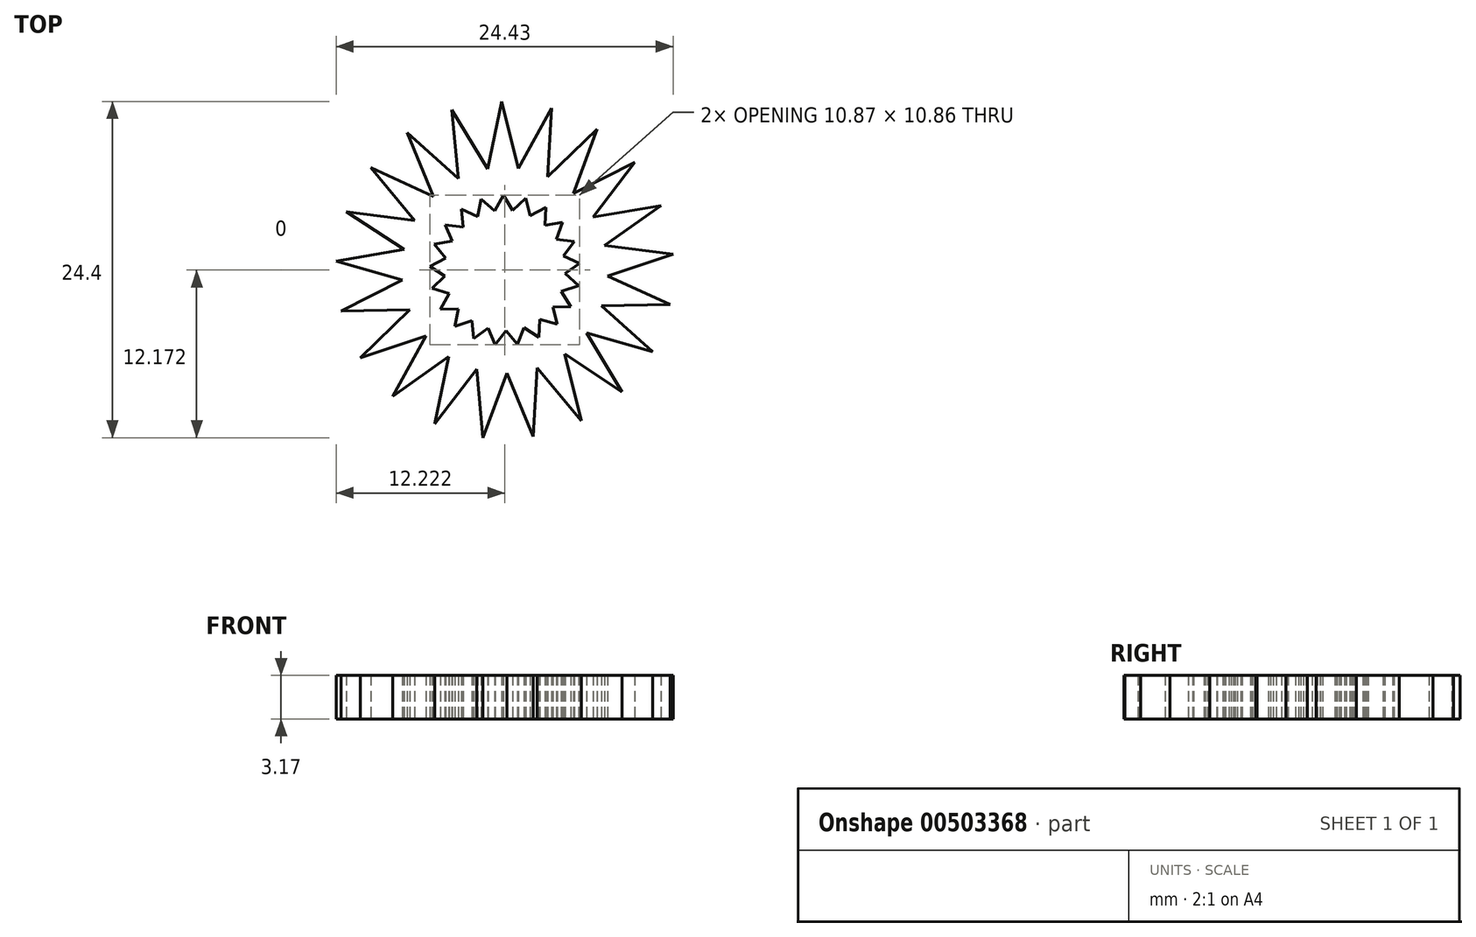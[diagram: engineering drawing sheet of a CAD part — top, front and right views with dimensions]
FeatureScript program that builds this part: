
annotation { "Feature Type Name" : "Feature", "Feature Type Description" : "" }
export const myFeature = defineFeature(function(context is Context, id is Id, definition is map)
    precondition{}
    {
        {
            var Q0;
            Q0=qCreatedBy(makeId("Top.planeOp"),FACE);
            var sketch = newSketch(context, id + "F0", { "sketchPlane" : qUnion([Q0])});
            skLineSegment(sketch, "E0", {"start": v(-5.1, -11.14) * mm, "end": v(-0.24, 12.25) * mm});
            skLineSegment(sketch, "E1", {"start": v(-0.24, 12.25) * mm, "end": v(5.54, -10.93) * mm});
            skLineSegment(sketch, "E2", {"start": v(5.54, -10.93) * mm, "end": v(-9.73, 7.45) * mm});
            skLineSegment(sketch, "E3", {"start": v(-9.73, 7.45) * mm, "end": v(12, -2.49) * mm});
            skLineSegment(sketch, "E4", {"start": v(12, -2.49) * mm, "end": v(-11.89, -2.96) * mm});
            skLineSegment(sketch, "E5", {"start": v(-11.89, -2.96) * mm, "end": v(9.43, 7.83) * mm});
            skLineSegment(sketch, "E6", {"start": v(9.43, 7.83) * mm, "end": v(-5.1, -11.14) * mm});
            skLineSegment(sketch, "E7", {"start": v(-10.49, -6.34) * mm, "end": v(6.7, 10.26) * mm});
            skLineSegment(sketch, "E8", {"start": v(6.7, 10.26) * mm, "end": v(-1.58, -12.15) * mm});
            skLineSegment(sketch, "E9", {"start": v(-1.58, -12.15) * mm, "end": v(-3.84, 11.63) * mm});
            skLineSegment(sketch, "E10", {"start": v(-3.84, 11.63) * mm, "end": v(8.51, -8.81) * mm});
            skLineSegment(sketch, "E11", {"start": v(8.51, -8.81) * mm, "end": v(-11.5, 4.25) * mm});
            skLineSegment(sketch, "E12", {"start": v(-11.5, 4.25) * mm, "end": v(12.2, 1.16) * mm});
            skLineSegment(sketch, "E13", {"start": v(12.2, 1.16) * mm, "end": v(-10.49, -6.34) * mm});
            skLineSegment(sketch, "E14", {"start": v(-8.15, -9.15) * mm, "end": v(3.38, 11.78) * mm});
            skLineSegment(sketch, "E15", {"start": v(3.38, 11.78) * mm, "end": v(2.07, -12.08) * mm});
            skLineSegment(sketch, "E16", {"start": v(2.07, -12.08) * mm, "end": v(-7.1, 9.98) * mm});
            skLineSegment(sketch, "E17", {"start": v(-7.1, 9.98) * mm, "end": v(10.73, -5.91) * mm});
            skLineSegment(sketch, "E18", {"start": v(10.73, -5.91) * mm, "end": v(-12.23, 0.67) * mm});
            skLineSegment(sketch, "E19", {"start": v(-12.23, 0.67) * mm, "end": v(11.31, 4.7) * mm});
            skLineSegment(sketch, "E20", {"start": v(11.31, 4.7) * mm, "end": v(-8.15, -9.15) * mm});
            skSolve(sketch);
        }
        {
            var Q0;
            {var subQ0=sQuery(id+"F0.wireOp",EDGE,"E7");var subQ1=sQuery(id+"F0.wireOp",EDGE,"E4");var subQ2=makeQuery(id+"F0.imprint","INTERSECT",VERTEX,{"derivedFrom":[subQ1,subQ0]});Q0=makeQuery(id+"F0.imprint","IMPRINT",FACE,{"disambiguationData":[TD([[makeQuery(id+"F0.imprint","IMPRINT",EDGE,{"disambiguationData":[TD([[subQ2,1.0]])],"derivedFrom":subQ1}),1.0]])]});}
            var Q1;
            {var subQ0=sQuery(id+"F0.wireOp",EDGE,"E20");var subQ1=sQuery(id+"F0.wireOp",EDGE,"E0");var subQ2=makeQuery(id+"F0.imprint","INTERSECT",VERTEX,{"derivedFrom":[subQ1,subQ0]});Q1=makeQuery(id+"F0.imprint","IMPRINT",FACE,{"disambiguationData":[TD([[makeQuery(id+"F0.imprint","IMPRINT",EDGE,{"disambiguationData":[TD([[subQ2,-1.0]])],"derivedFrom":subQ1}),1.0]])]});}
            var Q2;
            {var subQ0=sQuery(id+"F0.wireOp",EDGE,"E6");var subQ1=sQuery(id+"F0.wireOp",EDGE,"E0");var subQ2=makeQuery(id+"F0.imprint","INTERSECT",VERTEX,{"derivedFrom":[subQ1,subQ0]});Q2=makeQuery(id+"F0.imprint","IMPRINT",FACE,{"disambiguationData":[TD([[makeQuery(id+"F0.imprint","IMPRINT",EDGE,{"disambiguationData":[TD([[subQ2,-1.0]])],"derivedFrom":subQ1}),-1.0]])]});}
            var Q3;
            {var subQ0=sQuery(id+"F0.wireOp",EDGE,"E9");var subQ1=sQuery(id+"F0.wireOp",EDGE,"E6");var subQ2=makeQuery(id+"F0.imprint","INTERSECT",VERTEX,{"derivedFrom":[subQ1,subQ0]});Q3=makeQuery(id+"F0.imprint","IMPRINT",FACE,{"disambiguationData":[TD([[makeQuery(id+"F0.imprint","IMPRINT",EDGE,{"disambiguationData":[TD([[subQ2,1.0]])],"derivedFrom":subQ1}),1.0]])]});}
            var Q4;
            {var subQ0=sQuery(id+"F0.wireOp",EDGE,"E2");var subQ1=sQuery(id+"F0.wireOp",EDGE,"E1");var subQ2=makeQuery(id+"F0.imprint","INTERSECT",VERTEX,{"derivedFrom":[subQ1,subQ0]});Q4=makeQuery(id+"F0.imprint","IMPRINT",FACE,{"disambiguationData":[TD([[makeQuery(id+"F0.imprint","IMPRINT",EDGE,{"disambiguationData":[TD([[subQ2,1.0]])],"derivedFrom":subQ1}),-1.0]])]});}
            var Q5;
            {var subQ0=sQuery(id+"F0.wireOp",EDGE,"E11");var subQ1=sQuery(id+"F0.wireOp",EDGE,"E1");var subQ2=makeQuery(id+"F0.imprint","INTERSECT",VERTEX,{"derivedFrom":[subQ1,subQ0]});Q5=makeQuery(id+"F0.imprint","IMPRINT",FACE,{"disambiguationData":[TD([[makeQuery(id+"F0.imprint","IMPRINT",EDGE,{"disambiguationData":[TD([[subQ2,1.0]])],"derivedFrom":subQ1}),1.0]])]});}
            var Q6;
            {var subQ0=sQuery(id+"F0.wireOp",EDGE,"E17");var subQ1=sQuery(id+"F0.wireOp",EDGE,"E4");var subQ2=makeQuery(id+"F0.imprint","INTERSECT",VERTEX,{"derivedFrom":[subQ1,subQ0]});Q6=makeQuery(id+"F0.imprint","IMPRINT",FACE,{"disambiguationData":[TD([[makeQuery(id+"F0.imprint","IMPRINT",EDGE,{"disambiguationData":[TD([[subQ2,-1.0]])],"derivedFrom":subQ1}),1.0]])]});}
            var Q7;
            {var subQ0=sQuery(id+"F0.wireOp",EDGE,"E4");var subQ1=sQuery(id+"F0.wireOp",EDGE,"E3");var subQ2=makeQuery(id+"F0.imprint","INTERSECT",VERTEX,{"derivedFrom":[subQ1,subQ0]});Q7=makeQuery(id+"F0.imprint","IMPRINT",FACE,{"disambiguationData":[TD([[makeQuery(id+"F0.imprint","IMPRINT",EDGE,{"disambiguationData":[TD([[subQ2,1.0]])],"derivedFrom":subQ1}),-1.0]])]});}
            var Q8;
            {var subQ0=sQuery(id+"F0.wireOp",EDGE,"E13");var subQ1=sQuery(id+"F0.wireOp",EDGE,"E3");var subQ2=makeQuery(id+"F0.imprint","INTERSECT",VERTEX,{"derivedFrom":[subQ1,subQ0]});Q8=makeQuery(id+"F0.imprint","IMPRINT",FACE,{"disambiguationData":[TD([[makeQuery(id+"F0.imprint","IMPRINT",EDGE,{"disambiguationData":[TD([[subQ2,1.0]])],"derivedFrom":subQ1}),1.0]])]});}
            var Q9;
            {var subQ0=sQuery(id+"F0.wireOp",EDGE,"E19");var subQ1=sQuery(id+"F0.wireOp",EDGE,"E6");var subQ2=makeQuery(id+"F0.imprint","INTERSECT",VERTEX,{"derivedFrom":[subQ1,subQ0]});Q9=makeQuery(id+"F0.imprint","IMPRINT",FACE,{"disambiguationData":[TD([[makeQuery(id+"F0.imprint","IMPRINT",EDGE,{"disambiguationData":[TD([[subQ2,-1.0]])],"derivedFrom":subQ1}),1.0]])]});}
            var Q10;
            {var subQ0=sQuery(id+"F0.wireOp",EDGE,"E6");var subQ1=sQuery(id+"F0.wireOp",EDGE,"E5");var subQ2=makeQuery(id+"F0.imprint","INTERSECT",VERTEX,{"derivedFrom":[subQ1,subQ0]});Q10=makeQuery(id+"F0.imprint","IMPRINT",FACE,{"disambiguationData":[TD([[makeQuery(id+"F0.imprint","IMPRINT",EDGE,{"disambiguationData":[TD([[subQ2,1.0]])],"derivedFrom":subQ1}),-1.0]])]});}
            var Q11;
            {var subQ0=sQuery(id+"F0.wireOp",EDGE,"E8");var subQ1=sQuery(id+"F0.wireOp",EDGE,"E5");var subQ2=makeQuery(id+"F0.imprint","INTERSECT",VERTEX,{"derivedFrom":[subQ1,subQ0]});Q11=makeQuery(id+"F0.imprint","IMPRINT",FACE,{"disambiguationData":[TD([[makeQuery(id+"F0.imprint","IMPRINT",EDGE,{"disambiguationData":[TD([[subQ2,1.0]])],"derivedFrom":subQ1}),1.0]])]});}
            var Q12;
            {var subQ0=sQuery(id+"F0.wireOp",EDGE,"E14");var subQ1=sQuery(id+"F0.wireOp",EDGE,"E1");var subQ2=makeQuery(id+"F0.imprint","INTERSECT",VERTEX,{"derivedFrom":[subQ1,subQ0]});Q12=makeQuery(id+"F0.imprint","IMPRINT",FACE,{"disambiguationData":[TD([[makeQuery(id+"F0.imprint","IMPRINT",EDGE,{"disambiguationData":[TD([[subQ2,-1.0]])],"derivedFrom":subQ1}),1.0]])]});}
            var Q13;
            {var subQ0=sQuery(id+"F0.wireOp",EDGE,"E1");var subQ1=sQuery(id+"F0.wireOp",EDGE,"E0");var subQ2=makeQuery(id+"F0.imprint","INTERSECT",VERTEX,{"derivedFrom":[subQ1,subQ0]});Q13=makeQuery(id+"F0.imprint","IMPRINT",FACE,{"disambiguationData":[TD([[makeQuery(id+"F0.imprint","IMPRINT",EDGE,{"disambiguationData":[TD([[subQ2,1.0]])],"derivedFrom":subQ1}),-1.0]])]});}
            var Q14;
            {var subQ0=sQuery(id+"F0.wireOp",EDGE,"E10");var subQ1=sQuery(id+"F0.wireOp",EDGE,"E0");var subQ2=makeQuery(id+"F0.imprint","INTERSECT",VERTEX,{"derivedFrom":[subQ1,subQ0]});Q14=makeQuery(id+"F0.imprint","IMPRINT",FACE,{"disambiguationData":[TD([[makeQuery(id+"F0.imprint","IMPRINT",EDGE,{"disambiguationData":[TD([[subQ2,1.0]])],"derivedFrom":subQ1}),1.0]])]});}
            var Q15;
            {var subQ0=sQuery(id+"F0.wireOp",EDGE,"E16");var subQ1=sQuery(id+"F0.wireOp",EDGE,"E3");var subQ2=makeQuery(id+"F0.imprint","INTERSECT",VERTEX,{"derivedFrom":[subQ1,subQ0]});Q15=makeQuery(id+"F0.imprint","IMPRINT",FACE,{"disambiguationData":[TD([[makeQuery(id+"F0.imprint","IMPRINT",EDGE,{"disambiguationData":[TD([[subQ2,-1.0]])],"derivedFrom":subQ1}),1.0]])]});}
            var Q16;
            {var subQ0=sQuery(id+"F0.wireOp",EDGE,"E3");var subQ1=sQuery(id+"F0.wireOp",EDGE,"E2");var subQ2=makeQuery(id+"F0.imprint","INTERSECT",VERTEX,{"derivedFrom":[subQ1,subQ0]});Q16=makeQuery(id+"F0.imprint","IMPRINT",FACE,{"disambiguationData":[TD([[makeQuery(id+"F0.imprint","IMPRINT",EDGE,{"disambiguationData":[TD([[subQ2,1.0]])],"derivedFrom":subQ1}),-1.0]])]});}
            var Q17;
            {var subQ0=sQuery(id+"F0.wireOp",EDGE,"E12");var subQ1=sQuery(id+"F0.wireOp",EDGE,"E2");var subQ2=makeQuery(id+"F0.imprint","INTERSECT",VERTEX,{"derivedFrom":[subQ1,subQ0]});Q17=makeQuery(id+"F0.imprint","IMPRINT",FACE,{"disambiguationData":[TD([[makeQuery(id+"F0.imprint","IMPRINT",EDGE,{"disambiguationData":[TD([[subQ2,1.0]])],"derivedFrom":subQ1}),1.0]])]});}
            var Q18;
            {var subQ0=sQuery(id+"F0.wireOp",EDGE,"E18");var subQ1=sQuery(id+"F0.wireOp",EDGE,"E5");var subQ2=makeQuery(id+"F0.imprint","INTERSECT",VERTEX,{"derivedFrom":[subQ1,subQ0]});Q18=makeQuery(id+"F0.imprint","IMPRINT",FACE,{"disambiguationData":[TD([[makeQuery(id+"F0.imprint","IMPRINT",EDGE,{"disambiguationData":[TD([[subQ2,-1.0]])],"derivedFrom":subQ1}),1.0]])]});}
            var Q19;
            {var subQ0=sQuery(id+"F0.wireOp",EDGE,"E5");var subQ1=sQuery(id+"F0.wireOp",EDGE,"E4");var subQ2=makeQuery(id+"F0.imprint","INTERSECT",VERTEX,{"derivedFrom":[subQ1,subQ0]});Q19=makeQuery(id+"F0.imprint","IMPRINT",FACE,{"disambiguationData":[TD([[makeQuery(id+"F0.imprint","IMPRINT",EDGE,{"disambiguationData":[TD([[subQ2,1.0]])],"derivedFrom":subQ1}),-1.0]])]});}
            var Q20;
            {var subQ0=sQuery(id+"F0.wireOp",EDGE,"E7");var subQ1=sQuery(id+"F0.wireOp",EDGE,"E4");var subQ2=makeQuery(id+"F0.imprint","INTERSECT",VERTEX,{"derivedFrom":[subQ1,subQ0]});Q20=makeQuery(id+"F0.imprint","IMPRINT",FACE,{"disambiguationData":[TD([[makeQuery(id+"F0.imprint","IMPRINT",EDGE,{"disambiguationData":[TD([[subQ2,1.0]])],"derivedFrom":subQ1}),-1.0]])]});}
            var Q21;
            {var subQ0=sQuery(id+"F0.wireOp",EDGE,"E13");var subQ1=sQuery(id+"F0.wireOp",EDGE,"E0");var subQ2=makeQuery(id+"F0.imprint","INTERSECT",VERTEX,{"derivedFrom":[subQ1,subQ0]});Q21=makeQuery(id+"F0.imprint","IMPRINT",FACE,{"disambiguationData":[TD([[makeQuery(id+"F0.imprint","IMPRINT",EDGE,{"disambiguationData":[TD([[subQ2,-1.0]])],"derivedFrom":subQ1}),1.0]])]});}
            var Q22;
            {var subQ0=sQuery(id+"F0.wireOp",EDGE,"E20");var subQ1=sQuery(id+"F0.wireOp",EDGE,"E0");var subQ2=makeQuery(id+"F0.imprint","INTERSECT",VERTEX,{"derivedFrom":[subQ1,subQ0]});Q22=makeQuery(id+"F0.imprint","IMPRINT",FACE,{"disambiguationData":[TD([[makeQuery(id+"F0.imprint","IMPRINT",EDGE,{"disambiguationData":[TD([[subQ2,-1.0]])],"derivedFrom":subQ1}),-1.0]])]});}
            var Q23;
            {var subQ0=sQuery(id+"F0.wireOp",EDGE,"E9");var subQ1=sQuery(id+"F0.wireOp",EDGE,"E6");var subQ2=makeQuery(id+"F0.imprint","INTERSECT",VERTEX,{"derivedFrom":[subQ1,subQ0]});Q23=makeQuery(id+"F0.imprint","IMPRINT",FACE,{"disambiguationData":[TD([[makeQuery(id+"F0.imprint","IMPRINT",EDGE,{"disambiguationData":[TD([[subQ2,1.0]])],"derivedFrom":subQ1}),-1.0]])]});}
            var Q24;
            {var subQ0=sQuery(id+"F0.wireOp",EDGE,"E8");var subQ1=sQuery(id+"F0.wireOp",EDGE,"E2");var subQ2=makeQuery(id+"F0.imprint","INTERSECT",VERTEX,{"derivedFrom":[subQ1,subQ0]});Q24=makeQuery(id+"F0.imprint","IMPRINT",FACE,{"disambiguationData":[TD([[makeQuery(id+"F0.imprint","IMPRINT",EDGE,{"disambiguationData":[TD([[subQ2,-1.0]])],"derivedFrom":subQ1}),1.0]])]});}
            var Q25;
            {var subQ0=sQuery(id+"F0.wireOp",EDGE,"E15");var subQ1=sQuery(id+"F0.wireOp",EDGE,"E2");var subQ2=makeQuery(id+"F0.imprint","INTERSECT",VERTEX,{"derivedFrom":[subQ1,subQ0]});Q25=makeQuery(id+"F0.imprint","IMPRINT",FACE,{"disambiguationData":[TD([[makeQuery(id+"F0.imprint","IMPRINT",EDGE,{"disambiguationData":[TD([[subQ2,-1.0]])],"derivedFrom":subQ1}),1.0]])]});}
            var Q26;
            {var subQ0=sQuery(id+"F0.wireOp",EDGE,"E15");var subQ1=sQuery(id+"F0.wireOp",EDGE,"E2");var subQ2=makeQuery(id+"F0.imprint","INTERSECT",VERTEX,{"derivedFrom":[subQ1,subQ0]});Q26=makeQuery(id+"F0.imprint","IMPRINT",FACE,{"disambiguationData":[TD([[makeQuery(id+"F0.imprint","IMPRINT",EDGE,{"disambiguationData":[TD([[subQ2,-1.0]])],"derivedFrom":subQ1}),-1.0]])]});}
            var Q27;
            {var subQ0=sQuery(id+"F0.wireOp",EDGE,"E11");var subQ1=sQuery(id+"F0.wireOp",EDGE,"E1");var subQ2=makeQuery(id+"F0.imprint","INTERSECT",VERTEX,{"derivedFrom":[subQ1,subQ0]});Q27=makeQuery(id+"F0.imprint","IMPRINT",FACE,{"disambiguationData":[TD([[makeQuery(id+"F0.imprint","IMPRINT",EDGE,{"disambiguationData":[TD([[subQ2,1.0]])],"derivedFrom":subQ1}),-1.0]])]});}
            var Q28;
            {var subQ0=sQuery(id+"F0.wireOp",EDGE,"E4");var subQ1=sQuery(id+"F0.wireOp",EDGE,"E1");var subQ2=makeQuery(id+"F0.imprint","INTERSECT",VERTEX,{"derivedFrom":[subQ1,subQ0]});Q28=makeQuery(id+"F0.imprint","IMPRINT",FACE,{"disambiguationData":[TD([[makeQuery(id+"F0.imprint","IMPRINT",EDGE,{"disambiguationData":[TD([[subQ2,-1.0]])],"derivedFrom":subQ1}),1.0]])]});}
            var Q29;
            {var subQ0=sQuery(id+"F0.wireOp",EDGE,"E17");var subQ1=sQuery(id+"F0.wireOp",EDGE,"E4");var subQ2=makeQuery(id+"F0.imprint","INTERSECT",VERTEX,{"derivedFrom":[subQ1,subQ0]});Q29=makeQuery(id+"F0.imprint","IMPRINT",FACE,{"disambiguationData":[TD([[makeQuery(id+"F0.imprint","IMPRINT",EDGE,{"disambiguationData":[TD([[subQ2,-1.0]])],"derivedFrom":subQ1}),-1.0]])]});}
            var Q30;
            {var subQ0=sQuery(id+"F0.wireOp",EDGE,"E13");var subQ1=sQuery(id+"F0.wireOp",EDGE,"E3");var subQ2=makeQuery(id+"F0.imprint","INTERSECT",VERTEX,{"derivedFrom":[subQ1,subQ0]});Q30=makeQuery(id+"F0.imprint","IMPRINT",FACE,{"disambiguationData":[TD([[makeQuery(id+"F0.imprint","IMPRINT",EDGE,{"disambiguationData":[TD([[subQ2,1.0]])],"derivedFrom":subQ1}),-1.0]])]});}
            var Q31;
            {var subQ0=sQuery(id+"F0.wireOp",EDGE,"E6");var subQ1=sQuery(id+"F0.wireOp",EDGE,"E3");var subQ2=makeQuery(id+"F0.imprint","INTERSECT",VERTEX,{"derivedFrom":[subQ1,subQ0]});Q31=makeQuery(id+"F0.imprint","IMPRINT",FACE,{"disambiguationData":[TD([[makeQuery(id+"F0.imprint","IMPRINT",EDGE,{"disambiguationData":[TD([[subQ2,-1.0]])],"derivedFrom":subQ1}),1.0]])]});}
            var Q32;
            {var subQ0=sQuery(id+"F0.wireOp",EDGE,"E19");var subQ1=sQuery(id+"F0.wireOp",EDGE,"E6");var subQ2=makeQuery(id+"F0.imprint","INTERSECT",VERTEX,{"derivedFrom":[subQ1,subQ0]});Q32=makeQuery(id+"F0.imprint","IMPRINT",FACE,{"disambiguationData":[TD([[makeQuery(id+"F0.imprint","IMPRINT",EDGE,{"disambiguationData":[TD([[subQ2,-1.0]])],"derivedFrom":subQ1}),-1.0]])]});}
            var Q33;
            {var subQ0=sQuery(id+"F0.wireOp",EDGE,"E8");var subQ1=sQuery(id+"F0.wireOp",EDGE,"E5");var subQ2=makeQuery(id+"F0.imprint","INTERSECT",VERTEX,{"derivedFrom":[subQ1,subQ0]});Q33=makeQuery(id+"F0.imprint","IMPRINT",FACE,{"disambiguationData":[TD([[makeQuery(id+"F0.imprint","IMPRINT",EDGE,{"disambiguationData":[TD([[subQ2,1.0]])],"derivedFrom":subQ1}),-1.0]])]});}
            var Q34;
            {var subQ0=sQuery(id+"F0.wireOp",EDGE,"E7");var subQ1=sQuery(id+"F0.wireOp",EDGE,"E1");var subQ2=makeQuery(id+"F0.imprint","INTERSECT",VERTEX,{"derivedFrom":[subQ1,subQ0]});Q34=makeQuery(id+"F0.imprint","IMPRINT",FACE,{"disambiguationData":[TD([[makeQuery(id+"F0.imprint","IMPRINT",EDGE,{"disambiguationData":[TD([[subQ2,-1.0]])],"derivedFrom":subQ1}),1.0]])]});}
            var Q35;
            {var subQ0=sQuery(id+"F0.wireOp",EDGE,"E14");var subQ1=sQuery(id+"F0.wireOp",EDGE,"E1");var subQ2=makeQuery(id+"F0.imprint","INTERSECT",VERTEX,{"derivedFrom":[subQ1,subQ0]});Q35=makeQuery(id+"F0.imprint","IMPRINT",FACE,{"disambiguationData":[TD([[makeQuery(id+"F0.imprint","IMPRINT",EDGE,{"disambiguationData":[TD([[subQ2,-1.0]])],"derivedFrom":subQ1}),-1.0]])]});}
            var Q36;
            {var subQ0=sQuery(id+"F0.wireOp",EDGE,"E10");var subQ1=sQuery(id+"F0.wireOp",EDGE,"E0");var subQ2=makeQuery(id+"F0.imprint","INTERSECT",VERTEX,{"derivedFrom":[subQ1,subQ0]});Q36=makeQuery(id+"F0.imprint","IMPRINT",FACE,{"disambiguationData":[TD([[makeQuery(id+"F0.imprint","IMPRINT",EDGE,{"disambiguationData":[TD([[subQ2,1.0]])],"derivedFrom":subQ1}),-1.0]])]});}
            var Q37;
            {var subQ0=sQuery(id+"F0.wireOp",EDGE,"E3");var subQ1=sQuery(id+"F0.wireOp",EDGE,"E0");var subQ2=makeQuery(id+"F0.imprint","INTERSECT",VERTEX,{"derivedFrom":[subQ1,subQ0]});Q37=makeQuery(id+"F0.imprint","IMPRINT",FACE,{"disambiguationData":[TD([[makeQuery(id+"F0.imprint","IMPRINT",EDGE,{"disambiguationData":[TD([[subQ2,-1.0]])],"derivedFrom":subQ1}),1.0]])]});}
            var Q38;
            {var subQ0=sQuery(id+"F0.wireOp",EDGE,"E16");var subQ1=sQuery(id+"F0.wireOp",EDGE,"E3");var subQ2=makeQuery(id+"F0.imprint","INTERSECT",VERTEX,{"derivedFrom":[subQ1,subQ0]});Q38=makeQuery(id+"F0.imprint","IMPRINT",FACE,{"disambiguationData":[TD([[makeQuery(id+"F0.imprint","IMPRINT",EDGE,{"disambiguationData":[TD([[subQ2,-1.0]])],"derivedFrom":subQ1}),-1.0]])]});}
            var Q39;
            {var subQ0=sQuery(id+"F0.wireOp",EDGE,"E12");var subQ1=sQuery(id+"F0.wireOp",EDGE,"E2");var subQ2=makeQuery(id+"F0.imprint","INTERSECT",VERTEX,{"derivedFrom":[subQ1,subQ0]});Q39=makeQuery(id+"F0.imprint","IMPRINT",FACE,{"disambiguationData":[TD([[makeQuery(id+"F0.imprint","IMPRINT",EDGE,{"disambiguationData":[TD([[subQ2,1.0]])],"derivedFrom":subQ1}),-1.0]])]});}
            var Q40;
            {var subQ0=sQuery(id+"F0.wireOp",EDGE,"E5");var subQ1=sQuery(id+"F0.wireOp",EDGE,"E2");var subQ2=makeQuery(id+"F0.imprint","INTERSECT",VERTEX,{"derivedFrom":[subQ1,subQ0]});Q40=makeQuery(id+"F0.imprint","IMPRINT",FACE,{"disambiguationData":[TD([[makeQuery(id+"F0.imprint","IMPRINT",EDGE,{"disambiguationData":[TD([[subQ2,-1.0]])],"derivedFrom":subQ1}),1.0]])]});}
            var Q41;
            {var subQ0=sQuery(id+"F0.wireOp",EDGE,"E18");var subQ1=sQuery(id+"F0.wireOp",EDGE,"E5");var subQ2=makeQuery(id+"F0.imprint","INTERSECT",VERTEX,{"derivedFrom":[subQ1,subQ0]});Q41=makeQuery(id+"F0.imprint","IMPRINT",FACE,{"disambiguationData":[TD([[makeQuery(id+"F0.imprint","IMPRINT",EDGE,{"disambiguationData":[TD([[subQ2,-1.0]])],"derivedFrom":subQ1}),-1.0]])]});}
            extrude(context, id + "F1", {"entities" : qUnion([Q0, Q1, Q2, Q3, Q4, Q5, Q6, Q7, Q8, Q9, Q10, Q11, Q12, Q13, Q14, Q15, Q16, Q17, Q18, Q19, Q20, Q21, Q22, Q23, Q24, Q25, Q26, Q27, Q28, Q29, Q30, Q31, Q32, Q33, Q34, Q35, Q36, Q37, Q38, Q39, Q40, Q41]), "depth" : 3.17 * mm});
        }
    });
